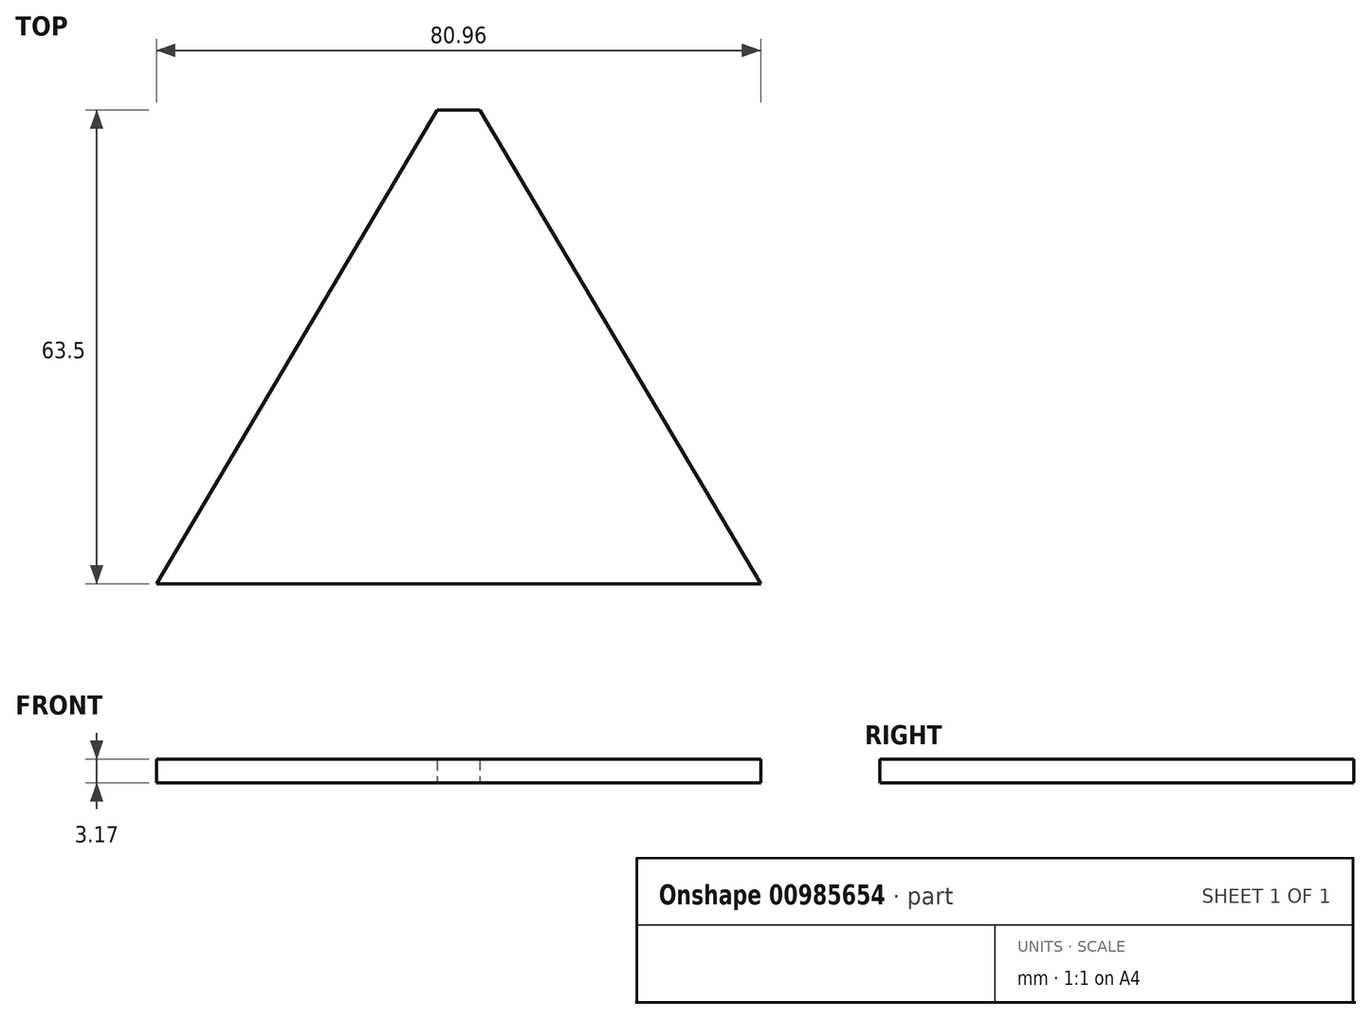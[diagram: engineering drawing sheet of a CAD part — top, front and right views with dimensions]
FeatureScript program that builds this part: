
annotation { "Feature Type Name" : "Feature", "Feature Type Description" : "" }
export const myFeature = defineFeature(function(context is Context, id is Id, definition is map)
    precondition{}
    {
        {
            var Q0;
            Q0=qCreatedBy(makeId("Top.planeOp"),FACE);
            var sketch = newSketch(context, id + "F0", { "sketchPlane" : qUnion([Q0])});
            skLineSegment(sketch, "E0", {"start": v(0, 0) * mm, "end": v(37.64, 63.5) * mm});
            skLineSegment(sketch, "E1", {"start": v(43.32, 63.5) * mm, "end": v(80.96, 0) * mm});
            skLineSegment(sketch, "E2", {"start": v(80.96, 0) * mm, "end": v(0, 0) * mm});
            skLineSegment(sketch, "E3", {"start": v(37.64, 63.5) * mm, "end": v(43.32, 63.5) * mm});
            skSolve(sketch);
        }
        {
            var Q0;
            Q0 = qSketchRegion(id + "F0", true);
            extrude(context, id + "F1", {"entities" : qUnion([Q0]), "depth" : 3.17 * mm, "offsetDistance" : 25.4 * mm});
        }
    });
